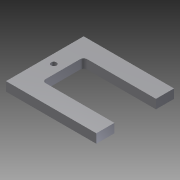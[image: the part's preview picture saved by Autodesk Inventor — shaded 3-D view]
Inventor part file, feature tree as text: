
AUTODESK INVENTOR PART (.ipt)
format: ipt  version: 2012 (Build 160160000, 160)  size: 86,016 bytes
history: native  units: mm
features: extrude x1, sketch x1
ambient origin geometry x8: Origin, YZ Plane, XZ Plane, XY Plane, X Axis, Y Axis, Z Axis, Center Point
feature tree (2):
  extrude  "Extrusion2"  Depth=5.0mm TaperAngle=0.0deg
  sketch  "Sketch1"  dims[d10=40.0mm d11=23.0mm d12=2.0mm d13=10.0mm d14=50.0mm d15=43.0mm d16=3.0mm d17=5.0mm d18=21.5mm d19=5.0mm d20=0.0mm]
